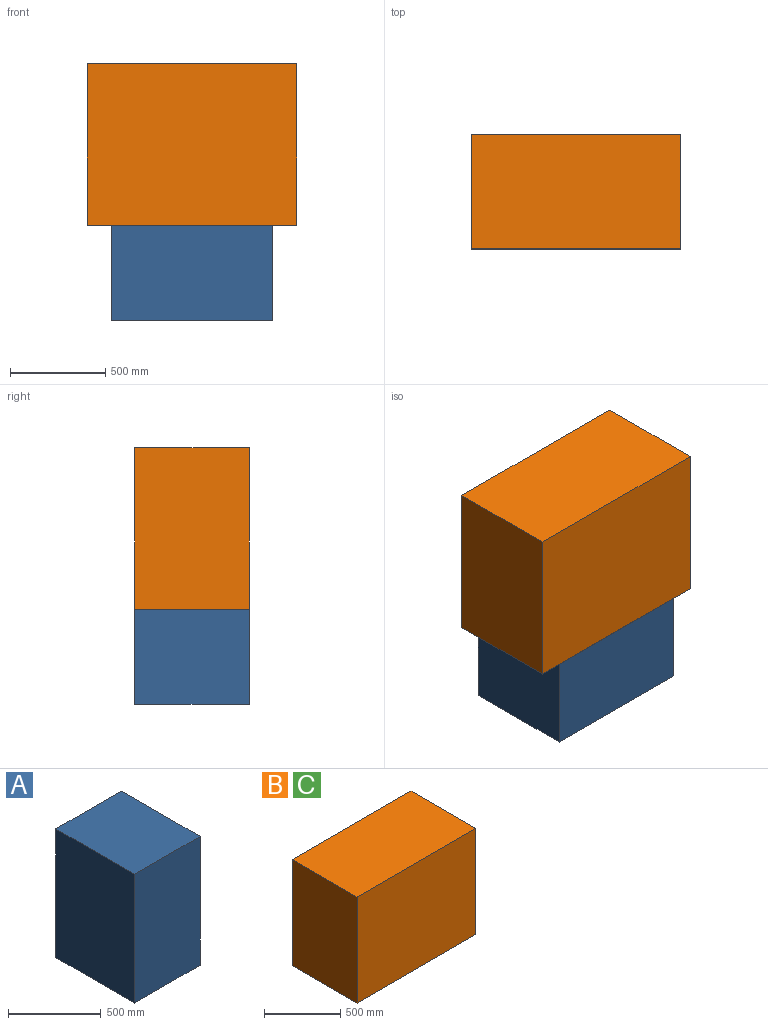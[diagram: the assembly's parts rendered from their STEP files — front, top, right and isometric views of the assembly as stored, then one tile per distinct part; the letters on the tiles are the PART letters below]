
ASSEMBLY  parts=3 mates=1
PART A: 6 faces, bbox 500x600x850 mm
  f0: plane 850x600mm, normal (-1,0,0), area 510000mm2, adj f1,f3,f4,f5
  f1: plane 600x500mm, normal (0,0,-1), area 300000mm2, adj f0,f2,f4,f5
  f2: plane 850x600mm, normal (1,0,0), area 510000mm2, adj f1,f3,f4,f5
  f3: plane 600x500mm, normal (0,0,1), area 300000mm2, adj f0,f2,f4,f5
  f4: plane 850x500mm, normal (0,-1,0), area 425000mm2, adj f0,f1,f2,f3
  f5: plane 850x500mm, normal (0,1,0), area 425000mm2, adj f0,f1,f2,f3
PART B: 6 faces, bbox 1100x600x850 mm
  f0: plane 850x600mm, normal (-1,0,0), area 510000mm2, adj f1,f3,f4,f5
  f1: plane 1100x600mm, normal (0,0,-1), area 660000mm2, adj f0,f2,f4,f5
  f2: plane 850x600mm, normal (1,0,0), area 510000mm2, adj f1,f3,f4,f5
  f3: plane 1100x600mm, normal (0,0,1), area 660000mm2, adj f0,f2,f4,f5
  f4: plane 1100x850mm, normal (0,-1,0), area 935000mm2, adj f0,f1,f2,f3
  f5: plane 1100x850mm, normal (0,1,0), area 935000mm2, adj f0,f1,f2,f3
PART C: same geometry as B
PLACE A rot(axis=(0.71,0,0.71),180deg) t=(6057.24,7456.16,-4712.05)mm
PLACE B t=(5932.24,8056.16,-4212.05)mm
PLACE C t=(5932.24,8056.16,-4212.05)mm
MATE parallel A.f2 <-> B.f1  axis (0,0,1) through (6482.24,7756.16,-4212.05)mm
